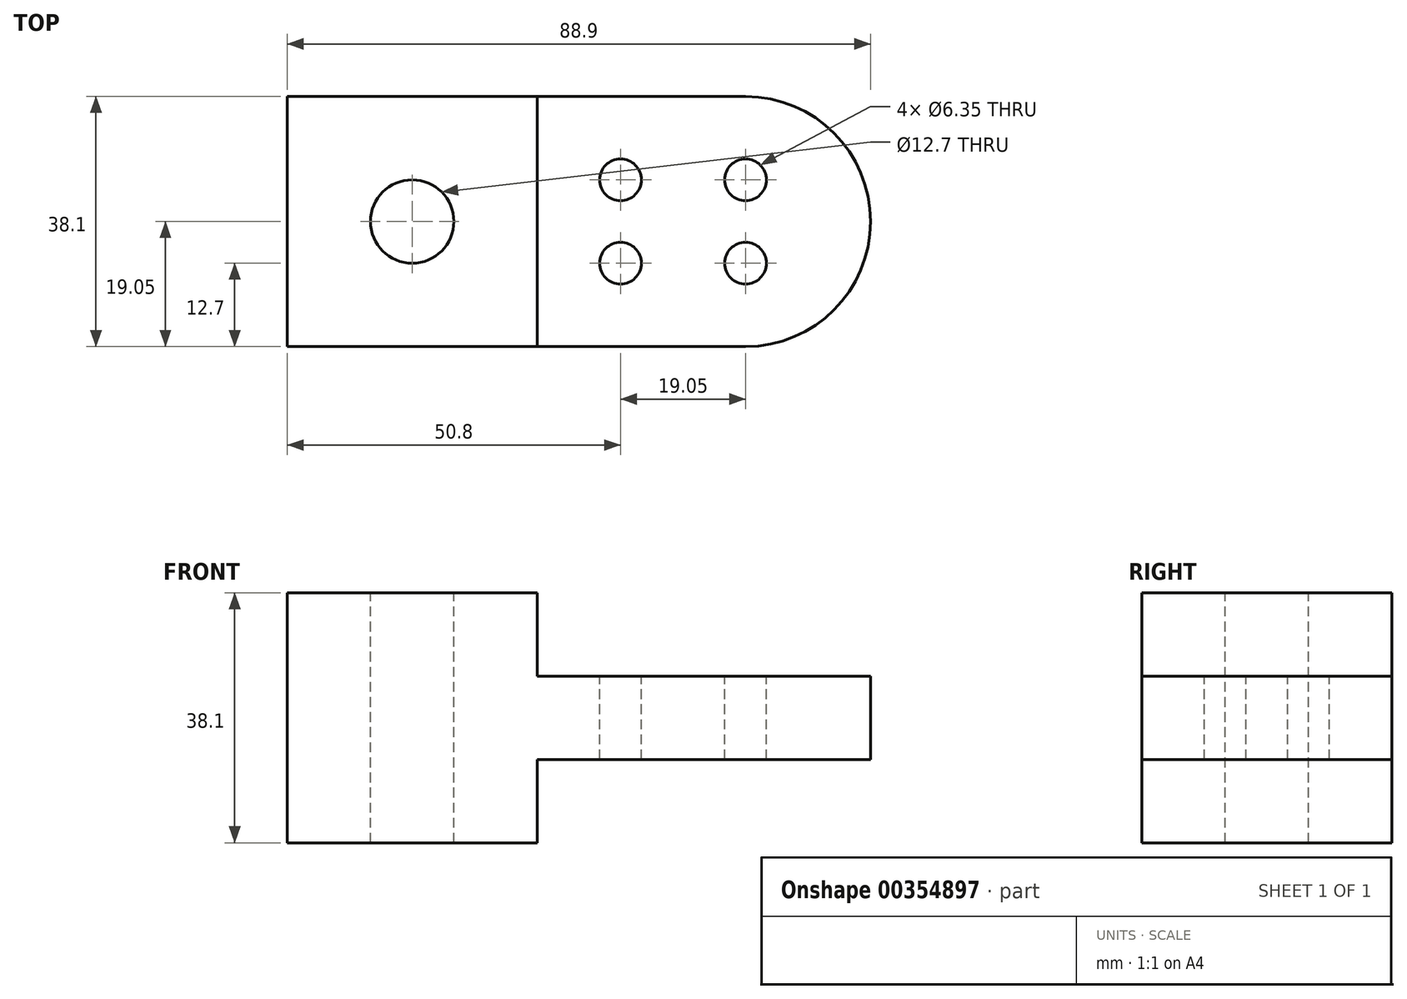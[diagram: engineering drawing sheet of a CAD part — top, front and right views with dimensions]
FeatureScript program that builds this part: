
annotation { "Feature Type Name" : "Feature", "Feature Type Description" : "" }
export const myFeature = defineFeature(function(context is Context, id is Id, definition is map)
    precondition{}
    {
        {
            var Q0;
            Q0=qCreatedBy(makeId("Front.planeOp"),FACE);
            var sketch = newSketch(context, id + "F0", { "sketchPlane" : qUnion([Q0])});
            skLineSegment(sketch, "E0", {"start": v(0, 0) * mm, "end": v(0, 38.1) * mm});
            skLineSegment(sketch, "E1", {"start": v(0, 38.1) * mm, "end": v(38.1, 38.1) * mm});
            skLineSegment(sketch, "E2", {"start": v(38.1, 38.1) * mm, "end": v(38.1, 25.4) * mm});
            skLineSegment(sketch, "E3", {"start": v(38.1, 25.4) * mm, "end": v(88.9, 25.4) * mm});
            skLineSegment(sketch, "E4", {"start": v(88.9, 25.4) * mm, "end": v(88.9, 12.7) * mm});
            skLineSegment(sketch, "E5", {"start": v(88.9, 12.7) * mm, "end": v(38.1, 12.7) * mm});
            skLineSegment(sketch, "E6", {"start": v(38.1, 12.7) * mm, "end": v(38.1, 0) * mm});
            skLineSegment(sketch, "E7", {"start": v(38.1, 0) * mm, "end": v(0, 0) * mm});
            skSolve(sketch);
        }
        {
            var Q0;
            Q0 = qSketchRegion(id + "F0", true);
            extrude(context, id + "F1", {"entities" : qUnion([Q0]), "depth" : 38.1 * mm});
        }
        {
            var Q0;
            Q0=makeQuery(id+"F1.opExtrude","SWEPT_FACE",FACE,{"disambiguationData":[OSD([sQuery(id+"F0.wireOp",EDGE,"E1")])]});
            var sketch = newSketch(context, id + "F2", { "sketchPlane" : qUnion([Q0])});
            skCircle(sketch, "E8", {"center": v(19.05, -19.05) * mm, "radius": 6.35 * mm});
            skPoint(sketch, "E8.centerSnap0", {"position": v(38.1, -19.05) * mm});
            skSolve(sketch);
        }
        {
            var Q0;
            Q0 = qSketchRegion(id + "F2", true);
            extrude(context, id + "F3", {"entities" : qUnion([Q0]), "operationType" : NewBodyOperationType.REMOVE, "oppositeDirection" : true, "depth" : 38.1 * mm});
        }
        {
            var Q0;
            Q0=makeQuery(id+"F1.opExtrude","SWEPT_FACE",FACE,{"disambiguationData":[OSD([sQuery(id+"F0.wireOp",EDGE,"E3")])]});
            var sketch = newSketch(context, id + "F4", { "sketchPlane" : qUnion([Q0])});
            skArc(sketch, "E9", {"start": v(69.85, -38.1) * mm, "mid": v(88.9, -19.05) * mm, "end": v(69.85, 0) * mm});
            skLineSegment(sketch, "E10", {"start": v(69.85, 0) * mm, "end": v(88.9, 0) * mm});
            skLineSegment(sketch, "E11", {"start": v(88.9, 0) * mm, "end": v(88.9, -38.1) * mm});
            skLineSegment(sketch, "E12", {"start": v(88.9, -38.1) * mm, "end": v(69.85, -38.1) * mm});
            skCircle(sketch, "E13", {"center": v(69.85, -12.7) * mm, "radius": 3.18 * mm});
            skCircle(sketch, "E14", {"center": v(50.8, -12.7) * mm, "radius": 3.18 * mm});
            skCircle(sketch, "E15", {"center": v(69.85, -25.4) * mm, "radius": 3.18 * mm});
            skCircle(sketch, "E16", {"center": v(50.8, -25.4) * mm, "radius": 3.18 * mm});
            skSolve(sketch);
        }
        {
            var Q0;
            Q0 = qSketchRegion(id + "F4", true);
            extrude(context, id + "F5", {"entities" : qUnion([Q0]), "operationType" : NewBodyOperationType.REMOVE, "oppositeDirection" : true, "depth" : 38.1 * mm});
        }
        {
            var Q0;
            Q0 = qSketchRegion(id + "F4", true);
            extrude(context, id + "F6", {"entities" : qUnion([Q0]), "operationType" : NewBodyOperationType.REMOVE, "oppositeDirection" : true, "depth" : 38.1 * mm});
        }
    });
